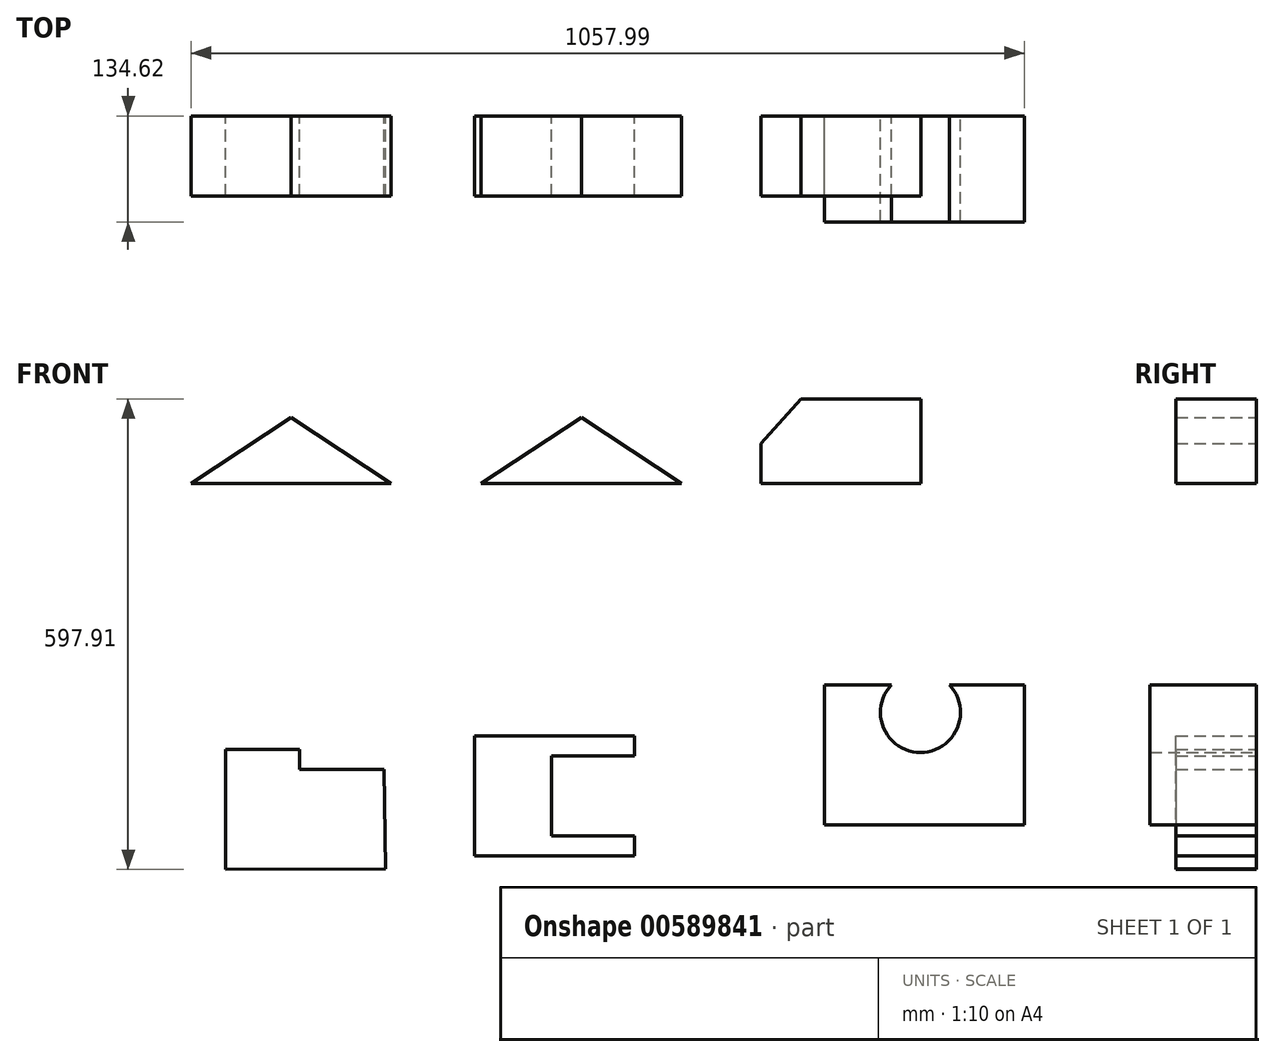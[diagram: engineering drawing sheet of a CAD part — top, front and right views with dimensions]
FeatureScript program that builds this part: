
annotation { "Feature Type Name" : "Feature", "Feature Type Description" : "" }
export const myFeature = defineFeature(function(context is Context, id is Id, definition is map)
    precondition{}
    {
        {
            var Q0;
            Q0=qCreatedBy(makeId("Front.planeOp"),FACE);
            var sketch = newSketch(context, id + "F0", { "sketchPlane" : qUnion([Q0])});
            skLineSegment(sketch, "E0", {"start": v(-127, 0) * mm, "end": v(0, 84.24) * mm});
            skLineSegment(sketch, "E1", {"start": v(0, 84.24) * mm, "end": v(127, 0) * mm});
            skLineSegment(sketch, "E2", {"start": v(127, 0) * mm, "end": v(-127, 0) * mm});
            skSolve(sketch);
        }
        {
            var Q0;
            Q0=makeQuery(id+"F0.imprint","IMPRINT",FACE,{"disambiguationData":[TD([[makeQuery(id+"F0.imprint","IMPRINT",EDGE,{"derivedFrom":sQuery(id+"F0.wireOp",EDGE,"E0")}),-1.0]])]});
            extrude(context, id + "F1", {"entities" : qUnion([Q0]), "depth" : 101.6 * mm, "offsetDistance" : 25.4 * mm});
        }
        {
            var Q0;
            Q0=qCreatedBy(makeId("Front.planeOp"),FACE);
            var sketch = newSketch(context, id + "F2", { "sketchPlane" : qUnion([Q0])});
            skLineSegment(sketch, "E3", {"start": v(241.36, 0) * mm, "end": v(495.36, 0) * mm});
            skLineSegment(sketch, "E4", {"start": v(495.36, 0) * mm, "end": v(368.36, 84.24) * mm});
            skLineSegment(sketch, "E5", {"start": v(368.36, 84.24) * mm, "end": v(241.36, 0) * mm});
            skSolve(sketch);
        }
        {
            var Q0;
            Q0=makeQuery(id+"F2.imprint","IMPRINT",FACE,{"disambiguationData":[TD([[makeQuery(id+"F2.imprint","IMPRINT",EDGE,{"derivedFrom":sQuery(id+"F2.wireOp",EDGE,"E3")}),1.0]])]});
            extrude(context, id + "F3", {"entities" : qUnion([Q0]), "depth" : 101.6 * mm, "offsetDistance" : 25.4 * mm});
        }
        {
            var Q0;
            Q0=qCreatedBy(makeId("Front.planeOp"),FACE);
            var sketch = newSketch(context, id + "F4", { "sketchPlane" : qUnion([Q0])});
            skLineSegment(sketch, "E6", {"start": v(596.38, 0) * mm, "end": v(596.38, 50.8) * mm});
            skLineSegment(sketch, "E7", {"start": v(596.38, 50.8) * mm, "end": v(647.18, 107.6) * mm});
            skLineSegment(sketch, "E8", {"start": v(647.18, 107.6) * mm, "end": v(697.98, 50.8) * mm});
            skLineSegment(sketch, "E9", {"start": v(697.98, 50.8) * mm, "end": v(697.98, 0) * mm});
            skLineSegment(sketch, "E10", {"start": v(697.98, 0) * mm, "end": v(596.38, 0) * mm});
            skLineSegment(sketch, "E11", {"start": v(647.18, 107.6) * mm, "end": v(799.58, 107.6) * mm});
            skLineSegment(sketch, "E12", {"start": v(799.58, 107.6) * mm, "end": v(799.58, 50.8) * mm});
            skLineSegment(sketch, "E13", {"start": v(799.58, 50.8) * mm, "end": v(697.98, 50.8) * mm});
            skLineSegment(sketch, "E14", {"start": v(799.58, 50.8) * mm, "end": v(799.58, 0) * mm});
            skLineSegment(sketch, "E15", {"start": v(799.58, 0) * mm, "end": v(697.98, 0) * mm});
            skSolve(sketch);
        }
        {
            var Q0;
            Q0=makeQuery(id+"F4.imprint","IMPRINT",FACE,{"disambiguationData":[TD([[makeQuery(id+"F4.imprint","IMPRINT",EDGE,{"derivedFrom":sQuery(id+"F4.wireOp",EDGE,"E6")}),-1.0]])]});
            var Q1;
            Q1=makeQuery(id+"F4.imprint","IMPRINT",FACE,{"disambiguationData":[TD([[makeQuery(id+"F4.imprint","IMPRINT",EDGE,{"derivedFrom":sQuery(id+"F4.wireOp",EDGE,"E8")}),1.0]])]});
            var Q2;
            Q2=makeQuery(id+"F4.imprint","IMPRINT",FACE,{"disambiguationData":[TD([[makeQuery(id+"F4.imprint","IMPRINT",EDGE,{"derivedFrom":sQuery(id+"F4.wireOp",EDGE,"E9")}),1.0]])]});
            extrude(context, id + "F5", {"entities" : qUnion([Q0, Q1, Q2]), "depth" : 101.6 * mm, "offsetDistance" : 25.4 * mm});
        }
        {
            var Q0;
            Q0=qCreatedBy(makeId("Front.planeOp"),FACE);
            var sketch = newSketch(context, id + "F6", { "sketchPlane" : qUnion([Q0])});
            skLineSegment(sketch, "E16", {"start": v(-83.48, -337.91) * mm, "end": v(-83.48, -490.31) * mm});
            skLineSegment(sketch, "E17", {"start": v(119.72, -489.36) * mm, "end": v(-83.48, -490.31) * mm});
            skLineSegment(sketch, "E18", {"start": v(-83.48, -337.91) * mm, "end": v(10.45, -337.91) * mm});
            skLineSegment(sketch, "E19", {"start": v(10.45, -337.91) * mm, "end": v(10.45, -363.31) * mm});
            skLineSegment(sketch, "E20", {"start": v(10.45, -363.31) * mm, "end": v(117.84, -363.31) * mm});
            skLineSegment(sketch, "E21", {"start": v(117.84, -363.31) * mm, "end": v(119.72, -489.36) * mm});
            skSolve(sketch);
        }
        {
            var Q0;
            Q0=makeQuery(id+"F6.imprint","IMPRINT",FACE,{"disambiguationData":[TD([[makeQuery(id+"F6.imprint","IMPRINT",EDGE,{"derivedFrom":sQuery(id+"F6.wireOp",EDGE,"E16")}),1.0]])]});
            extrude(context, id + "F7", {"entities" : qUnion([Q0]), "depth" : 101.6 * mm, "offsetDistance" : 25.4 * mm});
        }
        {
            var Q0;
            Q0=qCreatedBy(makeId("Front.planeOp"),FACE);
            var sketch = newSketch(context, id + "F8", { "sketchPlane" : qUnion([Q0])});
            skLineSegment(sketch, "E22.bottom", {"start": v(352.62, -473.4) * mm, "end": v(555.82, -473.4) * mm});
            skLineSegment(sketch, "E22.top", {"start": v(352.62, -321) * mm, "end": v(555.82, -321) * mm});
            skLineSegment(sketch, "E22.left", {"start": v(352.62, -473.4) * mm, "end": v(352.62, -321) * mm});
            skLineSegment(sketch, "E22.right", {"start": v(555.82, -473.4) * mm, "end": v(555.82, -321) * mm});
            skLineSegment(sketch, "E23", {"start": v(555.82, -346.4) * mm, "end": v(454.22, -346.4) * mm});
            skLineSegment(sketch, "E24", {"start": v(454.22, -346.4) * mm, "end": v(454.22, -448) * mm});
            skLineSegment(sketch, "E25", {"start": v(454.22, -448) * mm, "end": v(555.82, -448) * mm});
            skSolve(sketch);
        }
        {
            var Q0;
            {var subQ1=sQuery(id+"F8.wireOp",EDGE,"E22.bottom");Q0=makeQuery(id+"F8.imprint","IMPRINT",FACE,{"disambiguationData":[TD([[makeQuery(id+"F8.imprint","IMPRINT",EDGE,{"derivedFrom":subQ1}),1.0]])]});}
            extrude(context, id + "F9", {"entities" : qUnion([Q0]), "operationType" : NewBodyOperationType.REMOVE, "oppositeDirection" : true, "depth" : 101.6 * mm, "offsetDistance" : 25.4 * mm});
        }
        {
            var Q0;
            Q0=qCreatedBy(makeId("Front.planeOp"),FACE);
            var sketch = newSketch(context, id + "F10", { "sketchPlane" : qUnion([Q0])});
            skLineSegment(sketch, "E26.bottom", {"start": v(232.88, -472.75) * mm, "end": v(436.08, -472.75) * mm});
            skLineSegment(sketch, "E26.top", {"start": v(232.88, -320.35) * mm, "end": v(436.08, -320.35) * mm});
            skLineSegment(sketch, "E26.left", {"start": v(232.88, -472.75) * mm, "end": v(232.88, -320.35) * mm});
            skLineSegment(sketch, "E26.right", {"start": v(436.08, -472.75) * mm, "end": v(436.08, -320.35) * mm});
            skLineSegment(sketch, "E27", {"start": v(436.08, -345.75) * mm, "end": v(330.41, -345.75) * mm});
            skLineSegment(sketch, "E28", {"start": v(330.41, -345.75) * mm, "end": v(330.41, -447.35) * mm});
            skLineSegment(sketch, "E29", {"start": v(330.41, -447.35) * mm, "end": v(436.08, -447.35) * mm});
            skSolve(sketch);
        }
        {
            var Q0;
            {var subQ1=sQuery(id+"F10.wireOp",EDGE,"E26.bottom");Q0=makeQuery(id+"F10.imprint","IMPRINT",FACE,{"disambiguationData":[TD([[makeQuery(id+"F10.imprint","IMPRINT",EDGE,{"derivedFrom":subQ1}),1.0]])]});}
            extrude(context, id + "F11", {"entities" : qUnion([Q0]), "depth" : 101.6 * mm, "offsetDistance" : 25.4 * mm});
        }
        {
            var Q0;
            Q0=qCreatedBy(makeId("Front.planeOp"),FACE);
            var sketch = newSketch(context, id + "F12", { "sketchPlane" : qUnion([Q0])});
            skLineSegment(sketch, "E30.bottom", {"start": v(676.99, -433.5) * mm, "end": v(930.99, -433.5) * mm});
            skLineSegment(sketch, "E30.top", {"start": v(676.99, -255.7) * mm, "end": v(930.99, -255.7) * mm});
            skLineSegment(sketch, "E30.left", {"start": v(676.99, -433.5) * mm, "end": v(676.99, -255.7) * mm});
            skLineSegment(sketch, "E30.right", {"start": v(930.99, -433.5) * mm, "end": v(930.99, -255.7) * mm});
            skArc(sketch, "E31", {"start": v(762.41, -255.7) * mm, "mid": v(799.21, -341.5) * mm, "end": v(836.02, -255.7) * mm});
            skSolve(sketch);
        }
        {
            var Q0;
            Q0=makeQuery(id+"F12.imprint","IMPRINT",FACE,{"disambiguationData":[TD([[makeQuery(id+"F12.imprint","IMPRINT",EDGE,{"derivedFrom":sQuery(id+"F12.wireOp",EDGE,"E30.bottom")}),1.0]])]});
            extrude(context, id + "F13", {"entities" : qUnion([Q0]), "depth" : 134.62 * mm, "offsetDistance" : 25.4 * mm});
        }
    });
